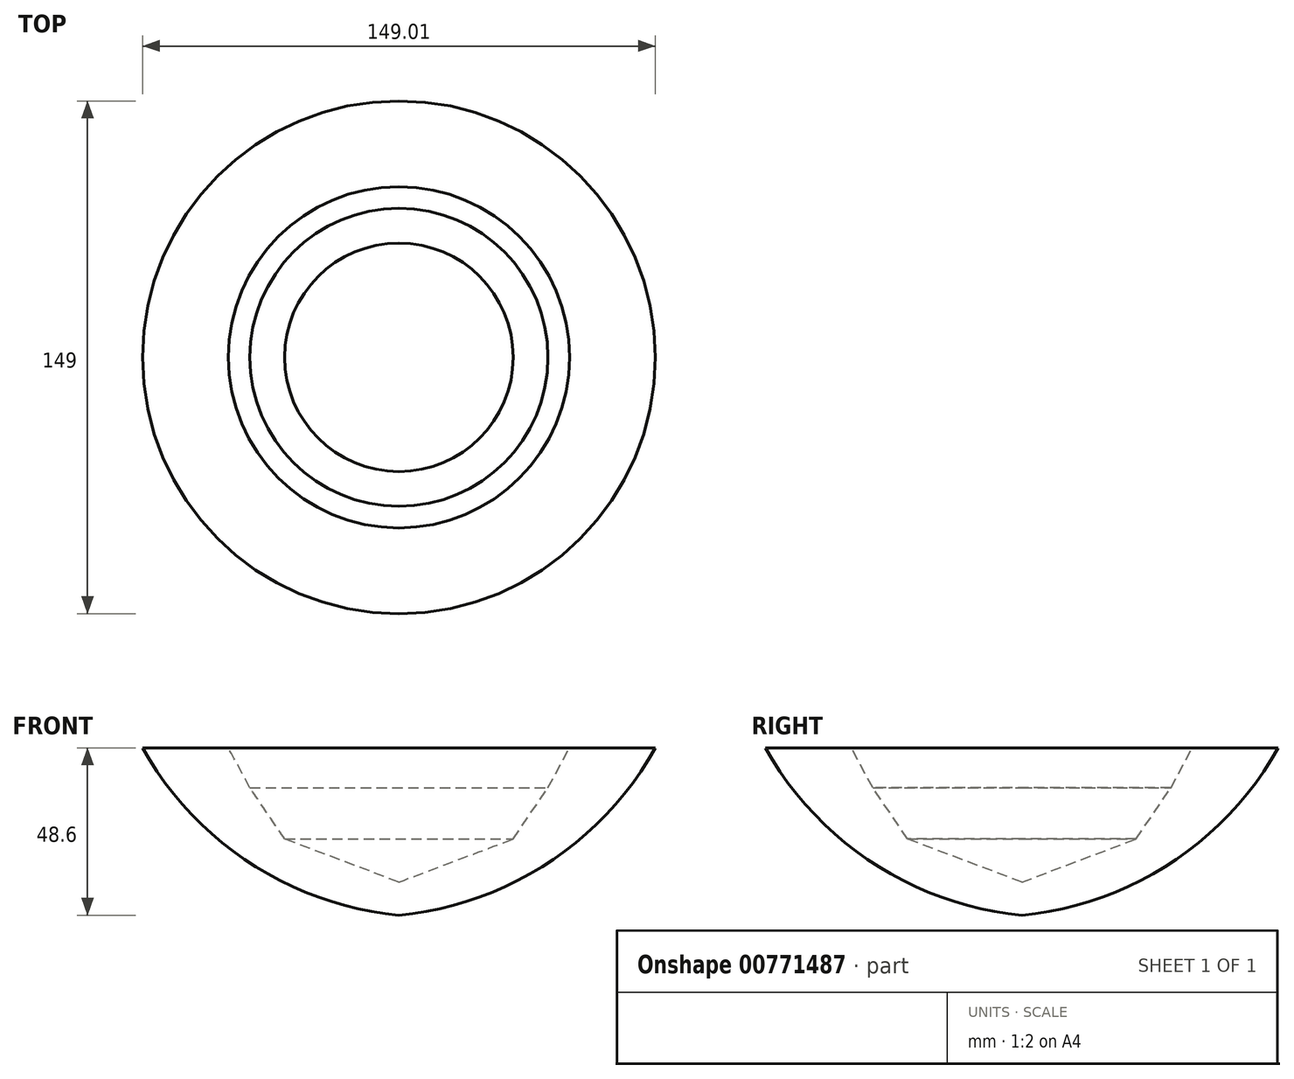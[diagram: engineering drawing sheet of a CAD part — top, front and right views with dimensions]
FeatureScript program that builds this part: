
annotation { "Feature Type Name" : "Feature", "Feature Type Description" : "" }
export const myFeature = defineFeature(function(context is Context, id is Id, definition is map)
    precondition{}
    {
        {
            var Q0;
            Q0=qCreatedBy(makeId("Front.planeOp"),FACE);
            var sketch = newSketch(context, id + "F0", { "sketchPlane" : qUnion([Q0])});
            skArc(sketch, "E0", {"start": v(-116.13, 56.3) * mm, "mid": v(-84.86, 22.82) * mm, "end": v(-41.62, 7.7) * mm});
            skLineSegment(sketch, "E1", {"start": v(-41.62, 7.7) * mm, "end": v(-41.62, 17.32) * mm});
            skLineSegment(sketch, "E2", {"start": v(-41.62, 17.32) * mm, "end": v(-74.83, 29.84) * mm});
            skLineSegment(sketch, "E3", {"start": v(-74.83, 29.84) * mm, "end": v(-84.93, 44.75) * mm});
            skLineSegment(sketch, "E4", {"start": v(-84.93, 44.75) * mm, "end": v(-91.19, 56.3) * mm});
            skLineSegment(sketch, "E5", {"start": v(-91.19, 56.3) * mm, "end": v(-116.13, 56.3) * mm});
            skSolve(sketch);
        }
        {
            var Q0;
            Q0 = qSketchRegion(id + "F0", true);
            var Q1;
            Q1=sQuery(id+"F0.wireOp",EDGE,"E1");
            revolve(context, id + "F1", {"surfaceOperationType" : NewSurfaceOperationType.NEW, "entities" : qUnion([Q0]), "axis" : qUnion([Q1]), "revolveType" : RevolveType.FULL});
        }
    });
